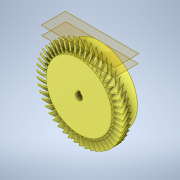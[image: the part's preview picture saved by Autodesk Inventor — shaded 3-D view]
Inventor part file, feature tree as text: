
AUTODESK INVENTOR PART (.ipt)
format: ipt  version: 2021.2 (Build 252289000, 289)  size: 3,002,880 bytes
history: native  units: in
note: dims shown in document units (in); Inventor stores cm internally (conversion verified against a paired STEP export)
features: sketch x5, extrude x4, plane x2, loft x1, pattern_circular x1, other x1
ambient origin geometry x8: Origin, YZ Plane, XZ Plane, XY Plane, X Axis, Y Axis, Z Axis, Center Point
bodies: Solid1 (feature_tree)
feature tree (14):
  extrude  "Extrusion1"  Depth=0.9688in
  plane  "Work Plane1"
  sketch  "Sketch2"  dims[d3=1.6in d4=0.0312in]
  plane  "Work Plane2"
  sketch  "Sketch4"  dims[d13=2.0in d38=0.315in]
  extrude  "Extrusion3"  Depth=0.0312in
  sketch  "Sketch6"  dims[d41=0.0in d42=0.0in d43=3.9375in d46=0.2in d47=0.0in d48=0.0in d49=90.0deg d50=0.0in d51=90.0deg d52=18.8976in d53=360.0deg d55=0.0in d56=0.0in d57=0.0625in d59=0.0625in]
  extrude  "Extrusion5"  Depth=0.315in
  loft  "Loft4"
  pattern_circular  "Circular Pattern7"  [2 undecoded]
  extrude  "Extrusion6"  Depth=0.2in TaperAngle=0.0deg
  sketch  "Sketch1"  dims[d0=3.0in d1=0.9688in d2=0.0777in]
  sketch  "Sketch5"  dims[d39=0.125in d40=0.125in]
  other  "Edges4"
note: 2 required parameter values undecoded (feature->parameter linkage not recoverable at this tier; creation-order binding heuristic only, values carry confidence <= 0.55)
